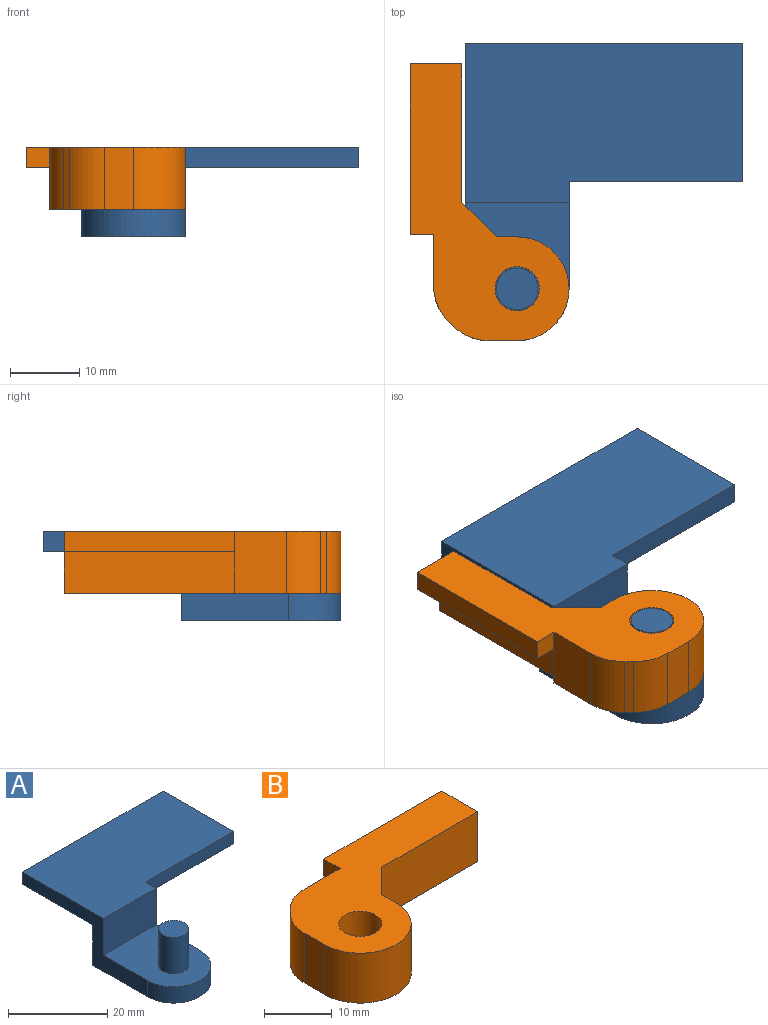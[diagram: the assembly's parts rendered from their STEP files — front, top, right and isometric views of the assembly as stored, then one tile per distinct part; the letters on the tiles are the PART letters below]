
ASSEMBLY  parts=2 mates=1
PART A: 14 faces, bbox 40x43x13 mm
  f0: plane 35.5x13mm, normal (-1,0,0), area 149mm2, adj f2,f5,f6,f7,f8,f9,f10,f12
  f1: plane 15.5x13mm, normal (1,0,0), area 89mm2, adj f3,f6,f7,f8,f9,f10,f12
  f2: plane 40x20mm, normal (0,0,-1), area 800mm2, adj f0,f3,f4,f5,f9
  f3: plane 25x3mm, normal (0,-1,0), area 75mm2, adj f1,f2,f4,f7
  f4: plane 20x3mm, normal (1,0,0), area 60mm2, adj f2,f3,f5,f7
  f5: plane 40x3mm, normal (0,1,0), area 120mm2, adj f0,f2,f4,f7
  f6: plane 15x9mm, normal (0,-1,0), area 135mm2, adj f0,f1,f7,f12
  f7: plane 40x23mm, normal (0,0,1), area 845mm2, adj f0,f1,f3,f4,f5,f6
  f8: cylinder r=7.5mm len=15mm, axis (0,0,1), area 94.2mm2, adj f0,f1,f10,f12
  f9: plane 15x10mm, normal (0,1,0), area 150mm2, adj f0,f1,f2,f10
  f10: plane 23x15mm, normal (0,0,-1), area 320.9mm2, adj f0,f1,f8,f9
  f11: cylinder r=3mm len=9mm, axis (0,0,1), area 169.6mm2, adj f12,f13
  f12: plane 20x15mm, normal (0,0,1), area 247.6mm2, adj f0,f1,f6,f8,f11
  f13: plane 6x6mm, normal (0,0,1), area 28.3mm2, adj f11
PART B: 18 faces, bbox 40x23x9 mm
  f0: plane 3.4x3mm, normal (-1,0,0), area 10.2mm2, adj f2,f6,f7,f11
  f1: plane 40x19.6mm, normal (0,0,-1), area 311mm2, adj f3,f4,f5,f7,f8,f9,f10,f12
  f2: plane 40x23mm, normal (0,0,1), area 421.7mm2, adj f0,f3,f4,f5,f6,f7,f8,f9
  f3: plane 9x3mm, normal (1,0,0), area 27mm2, adj f1,f2,f8,f14
  f4: plane 20x9mm, normal (0,-1,0), area 180mm2, adj f1,f2,f5,f14
  f5: plane 9x7.5mm, normal (1,0,0), area 40.5mm2, adj f1,f2,f4,f6,f11,f12
  f6: plane 24.6x3mm, normal (0,1,0), area 73.8mm2, adj f0,f2,f5,f11
  f7: plane 9x7.5mm, normal (0,1,0), area 67.5mm2, adj f0,f1,f2,f13,f16
  f8: cylinder r=7.5mm len=15mm, axis (0,0,-1), area 212.1mm2, adj f1,f2,f3,f9
  f9: plane 9x4.2mm, normal (-1,0,0), area 37.8mm2, adj f1,f2,f8,f17
  f10: cylinder r=3.2mm len=9mm, axis (0,0,-1), area 181mm2, adj f1,f2
  f11: plane 24.6x4.5mm, normal (0,0,-1), area 110.7mm2, adj f0,f5,f6,f12,f13
  f12: plane 24.6x6mm, normal (0,1,0), area 147.6mm2, adj f1,f5,f11,f13
  f13: plane 6x1.1mm, normal (1,0,0), area 6.6mm2, adj f1,f7,f11,f12
  f14: plane 9x5mm, normal (0.71,-0.71,0), area 63.6mm2, adj f1,f2,f3,f4
  f15: plane 9x0.9mm, normal (-0.71,0.71,0), area 11.4mm2, adj f1,f2,f16,f17
  f16: cylinder r=7mm len=9mm, axis (0,0,-1), area 49.5mm2, adj f1,f2,f7,f15
  f17: cylinder r=7mm len=9mm, axis (0,0,1), area 49.5mm2, adj f1,f2,f9,f15
PLACE A t=(267.5,275,-270)mm
PLACE B rot(axis=(0,0,1),90deg) t=(-290.5,252,-270)mm
MATE revolute A.f8 <-> B.f8  axis (0,0,1) through (0,-15.5,-1)mm
